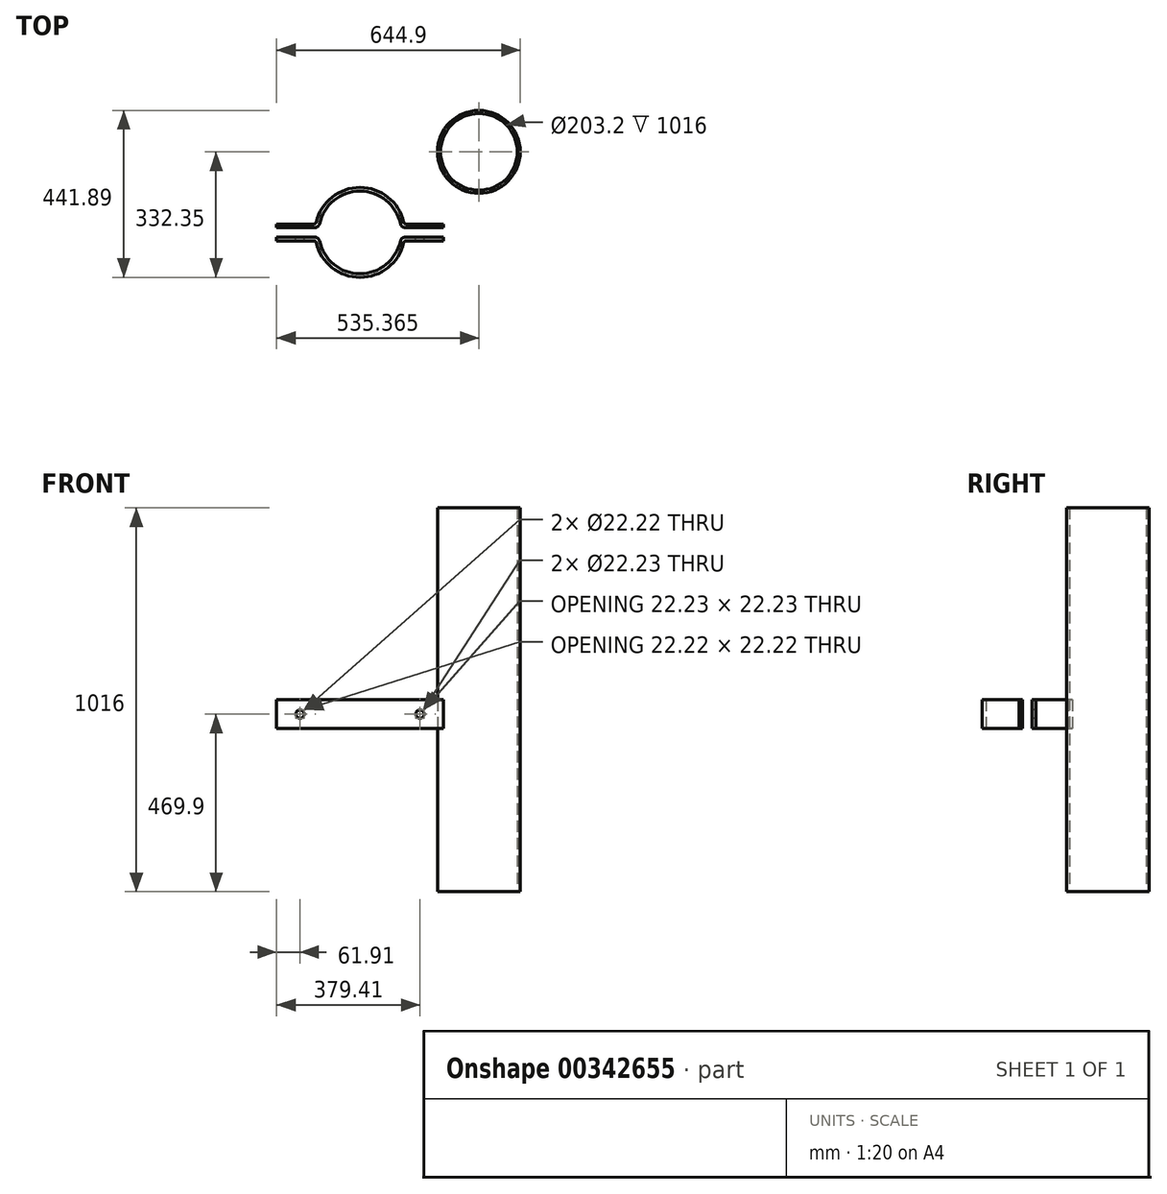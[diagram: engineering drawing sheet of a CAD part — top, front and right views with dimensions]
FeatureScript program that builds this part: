
annotation { "Feature Type Name" : "Feature", "Feature Type Description" : "" }
export const myFeature = defineFeature(function(context is Context, id is Id, definition is map)
    precondition{}
    {
        {
            var Q0;
            Q0=qCreatedBy(makeId("Top.planeOp"),FACE);
            var sketch = newSketch(context, id + "F0", { "sketchPlane" : qUnion([Q0])});
            skArc(sketch, "E0", {"start": v(-108.8, -12.7) * mm, "mid": v(0, -109.54) * mm, "end": v(108.8, -12.7) * mm});
            skArc(sketch, "E1", {"start": v(-116.97, -22.22) * mm, "mid": v(0, -119.06) * mm, "end": v(116.97, -22.22) * mm});
            skLineSegment(sketch, "E2", {"start": v(-220.66, 12.7) * mm, "end": v(-108.8, 12.7) * mm});
            skLineSegment(sketch, "E3", {"start": v(220.66, 12.7) * mm, "end": v(220.66, 22.23) * mm});
            skLineSegment(sketch, "E4", {"start": v(220.66, 22.22) * mm, "end": v(116.97, 22.22) * mm});
            skLineSegment(sketch, "E5", {"start": v(-220.66, 22.22) * mm, "end": v(-220.66, 12.7) * mm});
            skLineSegment(sketch, "E6.MirrorCS", {"start": v(-220.66, -12.7) * mm, "end": v(-108.8, -12.7) * mm});
            skLineSegment(sketch, "E7.MirrorCS", {"start": v(220.66, -22.22) * mm, "end": v(116.97, -22.22) * mm});
            skLineSegment(sketch, "E8.MirrorCS", {"start": v(220.66, -12.7) * mm, "end": v(220.66, -22.23) * mm});
            skLineSegment(sketch, "E9.MirrorCS", {"start": v(-220.66, -22.22) * mm, "end": v(-220.66, -12.7) * mm});
            skArc(sketch, "E10.trimOffspring", {"start": v(108.8, 12.7) * mm, "mid": v(0, 109.54) * mm, "end": v(-108.8, 12.7) * mm});
            skArc(sketch, "E11.trimOffspring", {"start": v(116.97, 22.22) * mm, "mid": v(0, 119.06) * mm, "end": v(-116.97, 22.22) * mm});
            skLineSegment(sketch, "E12.trimOffspring", {"start": v(108.8, 12.7) * mm, "end": v(220.66, 12.7) * mm});
            skLineSegment(sketch, "E13.trimOffspring", {"start": v(-116.97, 22.22) * mm, "end": v(-220.66, 22.22) * mm});
            skLineSegment(sketch, "E14.trimOffspring", {"start": v(108.8, -12.7) * mm, "end": v(220.66, -12.7) * mm});
            skLineSegment(sketch, "E15.trimOffspring", {"start": v(-116.97, -22.22) * mm, "end": v(-220.66, -22.22) * mm});
            skCircle(sketch, "E16", {"center": v(314.7, 213.3) * mm, "radius": 109.54 * mm});
            skCircle(sketch, "E17", {"center": v(314.7, 213.3) * mm, "radius": 101.6 * mm});
            skSolve(sketch);
        }
        {
            var Q0;
            Q0 = qSketchRegion(id + "F0", true);
            extrude(context, id + "F1", {"entities" : qUnion([Q0]), "endBound" : BoundingType.SYMMETRIC, "depth" : 76.2 * mm, "offsetDistance" : 25.4 * mm});
        }
        {
            var Q0;
            Q0=makeQuery(id+"F1.opExtrude","SWEPT_EDGE",EDGE,{"disambiguationData":[OSD([sQuery(id+"F0.wireOp",EDGE,"E11.trimOffspring"),sQuery(id+"F0.wireOp",EDGE,"E13.trimOffspring")])]});
            var Q1;
            Q1=makeQuery(id+"F1.opExtrude","SWEPT_EDGE",EDGE,{"disambiguationData":[OSD([sQuery(id+"F0.wireOp",EDGE,"E4"),sQuery(id+"F0.wireOp",EDGE,"E11.trimOffspring")])]});
            var Q2;
            Q2=makeQuery(id+"F1.opExtrude","SWEPT_EDGE",EDGE,{"disambiguationData":[OSD([sQuery(id+"F0.wireOp",EDGE,"E1"),sQuery(id+"F0.wireOp",EDGE,"E7.MirrorCS")])]});
            var Q3;
            Q3=makeQuery(id+"F1.opExtrude","SWEPT_EDGE",EDGE,{"disambiguationData":[OSD([sQuery(id+"F0.wireOp",EDGE,"E1"),sQuery(id+"F0.wireOp",EDGE,"E15.trimOffspring")])]});
            fillet(context, id + "F2", {"entities" : qUnion([Q0, Q1, Q2, Q3]), "radius" : 6.35 * mm, "tangentPropagation" : true, "allowEdgeOverflow" : false});
        }
        {
            var Q0;
            Q0=makeQuery(id+"F1.opExtrude","SWEPT_EDGE",EDGE,{"disambiguationData":[OSD([sQuery(id+"F0.wireOp",EDGE,"E2"),sQuery(id+"F0.wireOp",EDGE,"E10.trimOffspring")])]});
            var Q1;
            Q1=makeQuery(id+"F1.opExtrude","SWEPT_EDGE",EDGE,{"disambiguationData":[OSD([sQuery(id+"F0.wireOp",EDGE,"E10.trimOffspring"),sQuery(id+"F0.wireOp",EDGE,"E12.trimOffspring")])]});
            var Q2;
            Q2=makeQuery(id+"F1.opExtrude","SWEPT_EDGE",EDGE,{"disambiguationData":[OSD([sQuery(id+"F0.wireOp",EDGE,"E0"),sQuery(id+"F0.wireOp",EDGE,"E14.trimOffspring")])]});
            var Q3;
            Q3=makeQuery(id+"F1.opExtrude","SWEPT_EDGE",EDGE,{"disambiguationData":[OSD([sQuery(id+"F0.wireOp",EDGE,"E0"),sQuery(id+"F0.wireOp",EDGE,"E6.MirrorCS")])]});
            fillet(context, id + "F3", {"entities" : qUnion([Q0, Q1, Q2, Q3]), "radius" : 12.7 * mm, "tangentPropagation" : true, "allowEdgeOverflow" : false});
        }
        {
            var Q0;
            Q0=qCreatedBy(makeId("Front.planeOp"),FACE);
            var sketch = newSketch(context, id + "F4", { "sketchPlane" : qUnion([Q0])});
            skCircle(sketch, "E18", {"center": v(-158.75, 0) * mm, "radius": 11.1 * mm});
            skCircle(sketch, "E19", {"center": v(158.75, 0) * mm, "radius": 11.11 * mm});
            skSolve(sketch);
        }
        {
            var Q0;
            Q0 = qSketchRegion(id + "F4", true);
            extrude(context, id + "F5", {"entities" : qUnion([Q0]), "operationType" : NewBodyOperationType.REMOVE, "endBound" : BoundingType.THROUGH_ALL, "depth" : 25.4 * mm});
        }
        {
            var Q0;
            Q0=makeQuery(id+"F4.imprint","IMPRINT",FACE,{"disambiguationData":[TD([[makeQuery(id+"F4.imprint","IMPRINT",EDGE,{"derivedFrom":sQuery(id+"F4.wireOp",EDGE,"E18")}),1.0]])]});
            var Q1;
            Q1=makeQuery(id+"F4.imprint","IMPRINT",FACE,{"disambiguationData":[TD([[makeQuery(id+"F4.imprint","IMPRINT",EDGE,{"derivedFrom":sQuery(id+"F4.wireOp",EDGE,"E19")}),1.0]])]});
            extrude(context, id + "F6", {"entities" : qUnion([Q0, Q1]), "operationType" : NewBodyOperationType.REMOVE, "endBound" : BoundingType.THROUGH_ALL, "oppositeDirection" : true, "depth" : 25.4 * mm});
        }
        {
            var Q0;
            Q0=makeQuery(id+"F1.opExtrude","CAP_FACE",FACE,{"disambiguationData":[OSD([sQuery(id+"F0.wireOp",EDGE,"E16"),sQuery(id+"F0.wireOp",EDGE,"E17")])],"isStart":false});
            var Q1;
            Q1=sQuery(id+"F0.wireOp",EDGE,"E16");
            var Q2;
            Q2=sQuery(id+"F0.wireOp",EDGE,"E17");
            extrude(context, id + "F7", {"entities" : qUnion([Q0]), "operationType" : NewBodyOperationType.ADD, "surfaceEntities" : qUnion([Q1, Q2]), "endBound" : BoundingType.SYMMETRIC, "depth" : 1016 * mm});
        }
    });
